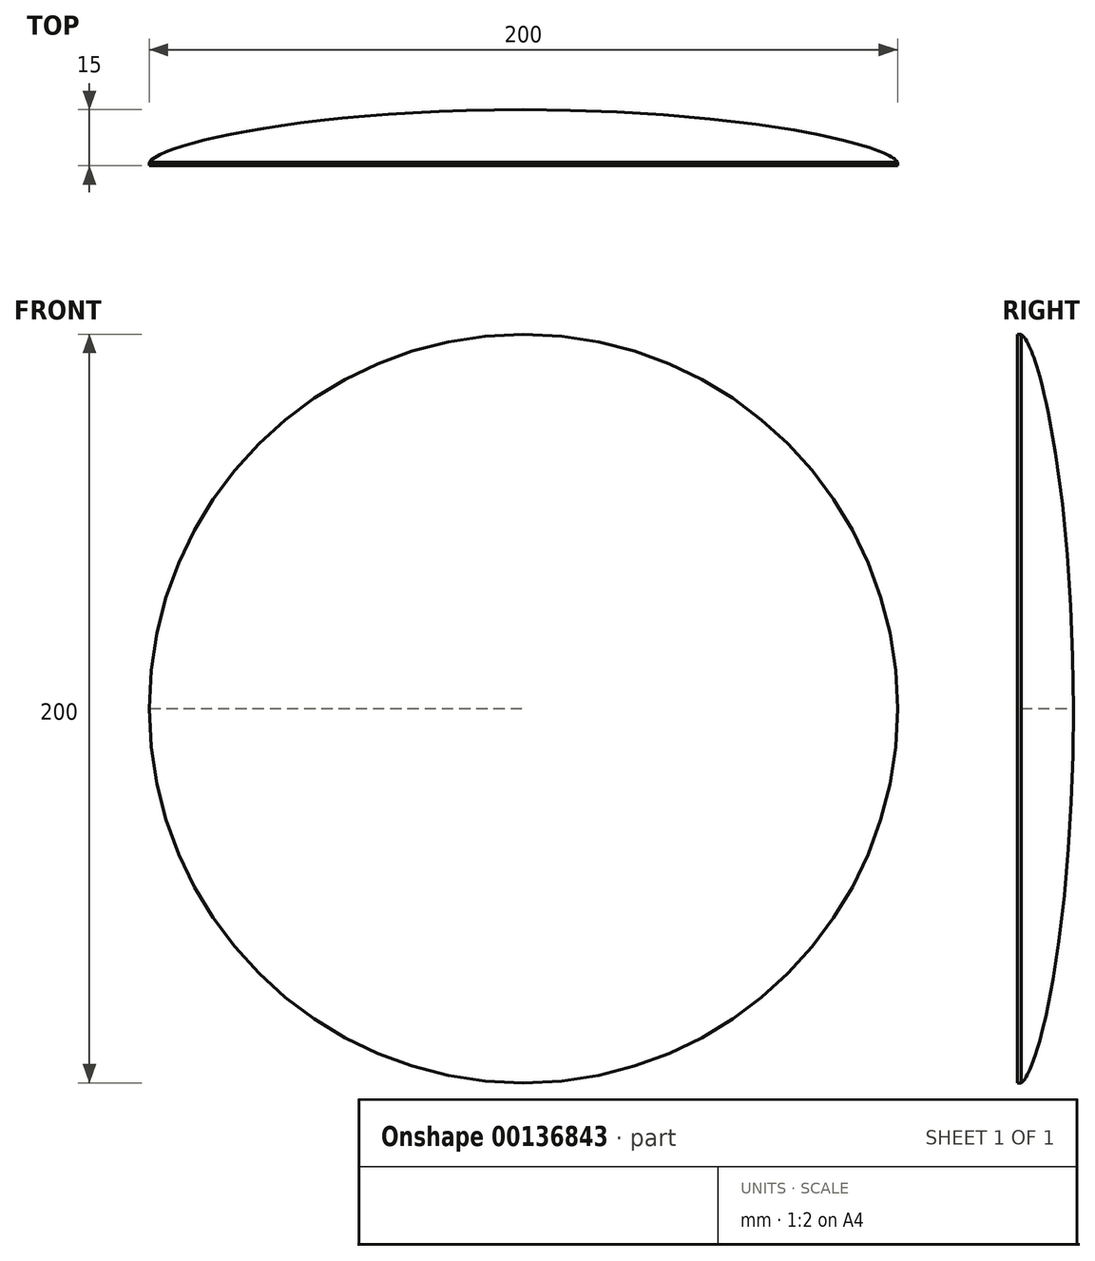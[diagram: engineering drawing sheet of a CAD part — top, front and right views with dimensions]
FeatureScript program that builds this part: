
annotation { "Feature Type Name" : "Feature", "Feature Type Description" : "" }
export const myFeature = defineFeature(function(context is Context, id is Id, definition is map)
    precondition{}
    {
        {
            var Q0;
            Q0=qCreatedBy(makeId("Top.planeOp"),FACE);
            var sketch = newSketch(context, id + "F0", { "sketchPlane" : qUnion([Q0])});
            skLineSegment(sketch, "E0", {"start": v(0, 0) * mm, "end": v(-100, 0) * mm});
            skLineSegment(sketch, "E1", {"start": v(-100, 0) * mm, "end": v(-100, 1) * mm});
            skLineSegment(sketch, "E2", {"start": v(0, 0) * mm, "end": v(0, 15) * mm});
            skFitSpline(sketch, "E3", {"points": [v(-100, 1) * mm, v(0, 15) * mm], "startDerivative": vector(8.14, 13.62) * mm, "endDerivative": vector(182.37, 0.49) * mm});
            skSolve(sketch);
        }
        {
            var Q0;
            Q0 = qSketchRegion(id + "F0", true);
            var Q1;
            Q1=sQuery(id+"F0.wireOp",EDGE,"E2");
            revolve(context, id + "F1", {"entities" : qUnion([Q0]), "axis" : qUnion([Q1]), "revolveType" : RevolveType.FULL});
        }
    });
